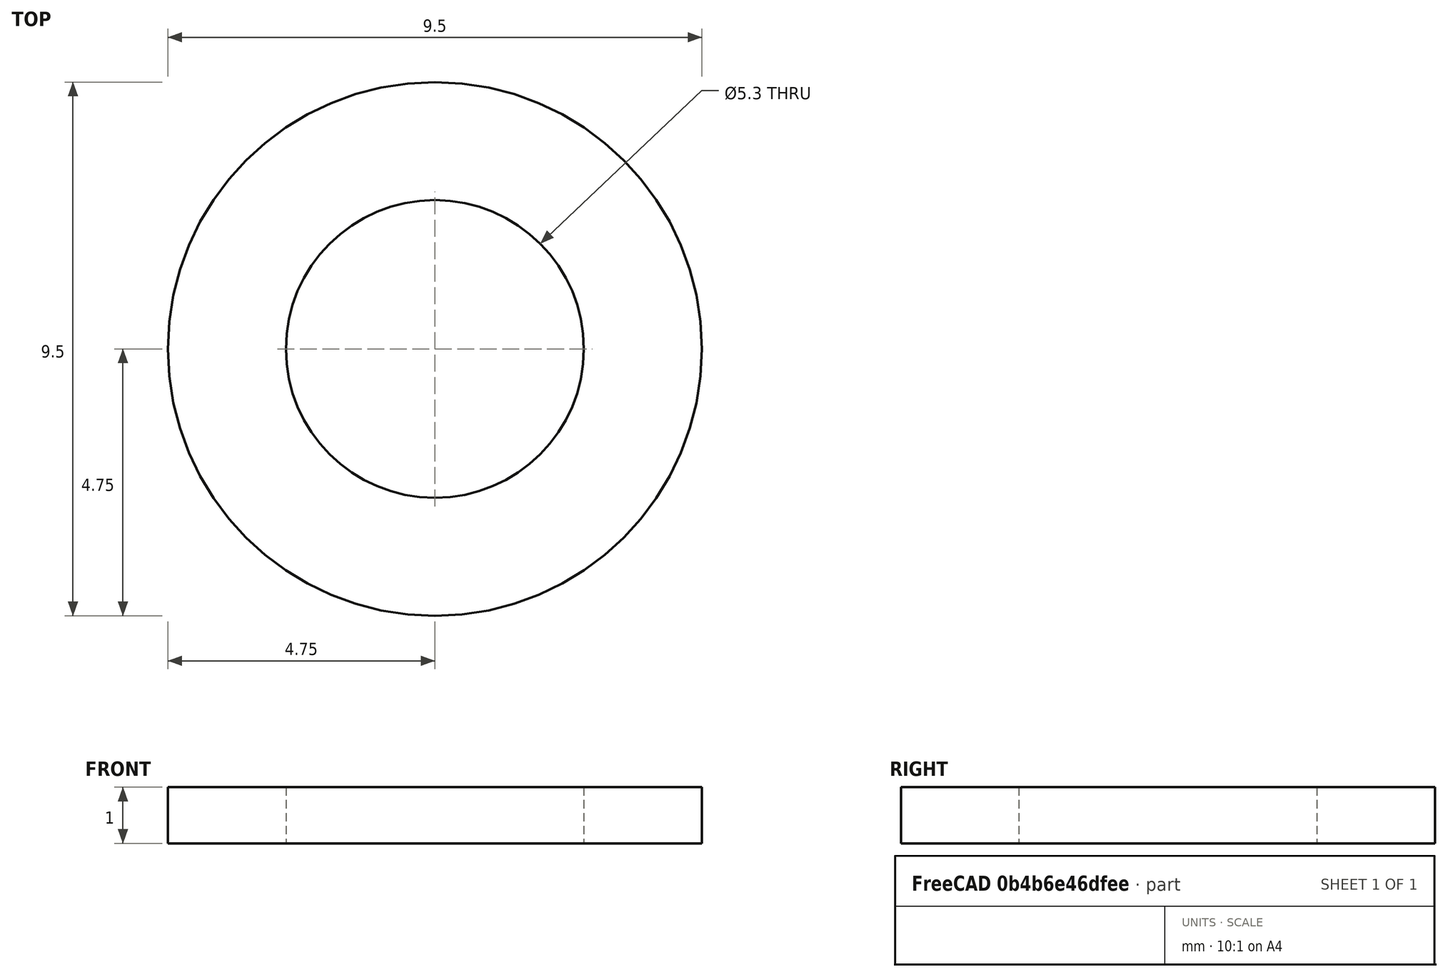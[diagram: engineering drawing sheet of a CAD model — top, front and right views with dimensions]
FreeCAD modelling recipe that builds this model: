
FCSTD DOCUMENT  (FreeCAD 0.14R3700 (Git))
Label: Scheibe DIN 433 - A 5,3
License: CC-BY 3.0
LicenseURL: http://creativecommons.org/licenses/by/3.0/
objects: Sketcher::SketchObject×1, PartDesign::Revolution×1, Part::Feature×1
note: 4 computed .brp shape members not serialized (recipe doc carries the construction recipe); baked Part::Feature solids carry a one-line shape summary decoded from their .brp

FEATURE [Sketcher::SketchObject] Sketch
  Placement = pos=(0,0,0) rot=(0.57735,0.57735,0.57735;2.0944rad)
  sketch-geometry (4):
    g0: LineSegment StartX=2.65 StartY=0 StartZ=0 EndX=4.75 EndY=0 EndZ=0
    g1: LineSegment StartX=4.75 StartY=0 StartZ=0 EndX=4.75 EndY=1 EndZ=0
    g2: LineSegment StartX=4.75 StartY=1 StartZ=0 EndX=2.65 EndY=1 EndZ=0
    g3: LineSegment StartX=2.65 StartY=1 StartZ=0 EndX=2.65 EndY=0 EndZ=0
  constraints (12):
    c: Coincident(g0,g1)
    c: Coincident(g1,g2)
    c: Coincident(g2,g3)
    c: Coincident(g3,g0)
    c: Horizontal(g0)
    c: Horizontal(g2)
    c: Vertical(g1)
    c: Vertical(g3)
    c: PointOnObject(g0,g-1)
    c: DistanceY(g1) = 1
    c: DistanceX(g-1,g2) = 2.65
    c: DistanceX(g-1,g1) = 4.75
FEATURE [PartDesign::Revolution] Revolution  label="Scheibe DIN 433 - A 5,3 #"
  Angle = 360
  Axis = (0,0,1)
  Base = (0,0,0)
  Placement = pos=(0,0,0) rot=(0.57735,0.57735,0.57735;2.0944rad)
  ReferenceAxis = -> Sketch [V_Axis]
  Reversed = true
  Sketch = -> Sketch
FEATURE [Part::Feature] Revolution001  label="Scheibe DIN 433 - A 5,3 #001"
  Placement = pos=(0,0,0) rot=(0.57735,0.57735,0.57735;2.0944rad)
  shape: bbox 9.5 x 9.5 x 1 mm, 4 faces (baked)
